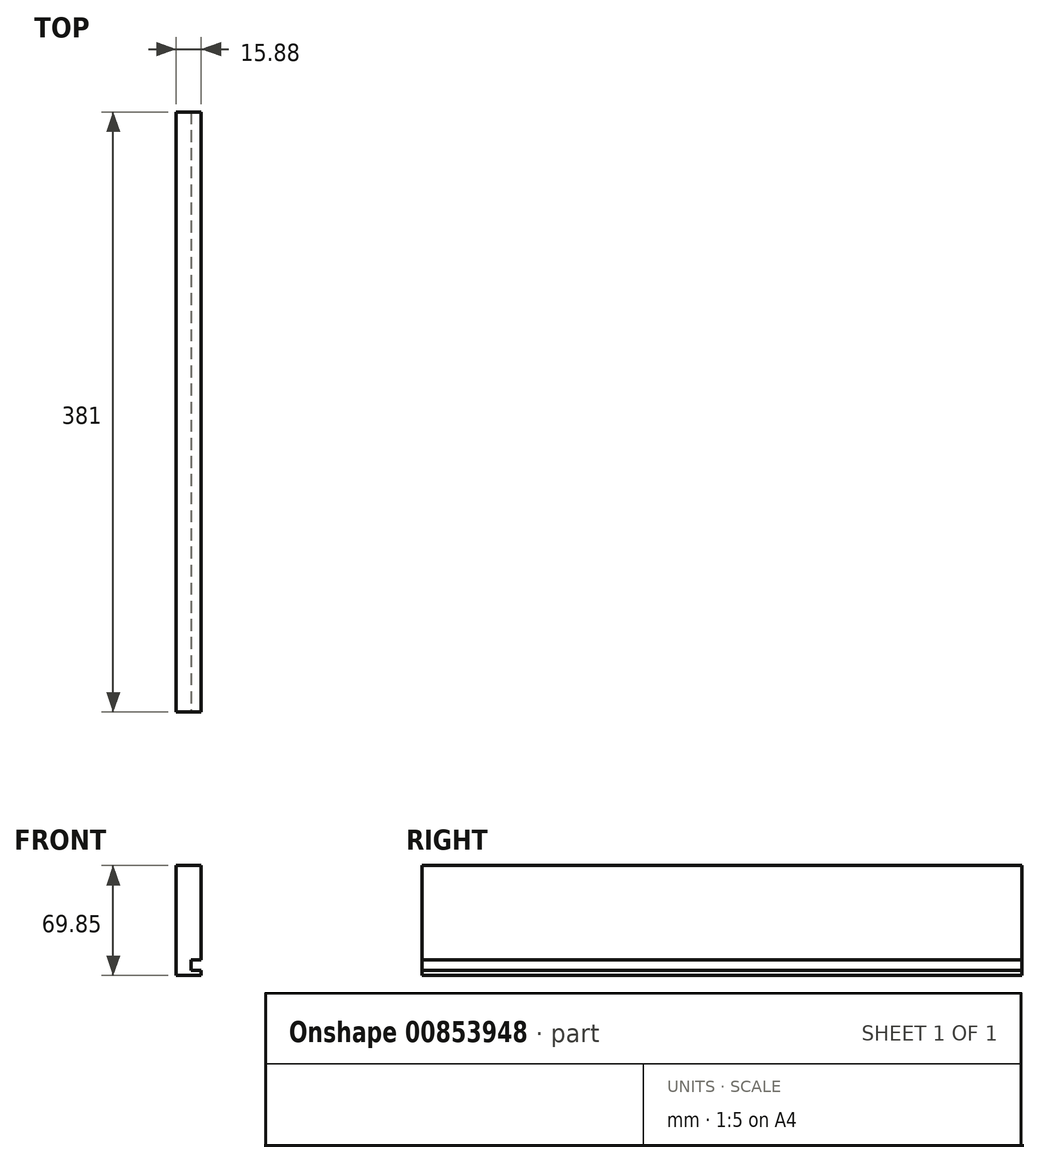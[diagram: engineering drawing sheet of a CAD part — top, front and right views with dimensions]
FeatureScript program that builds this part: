
annotation { "Feature Type Name" : "Feature", "Feature Type Description" : "" }
export const myFeature = defineFeature(function(context is Context, id is Id, definition is map)
    precondition{}
    {
        {
            var Q0;
            Q0=qCreatedBy(makeId("Right.planeOp"),FACE);
            var sketch = newSketch(context, id + "F0", { "sketchPlane" : qUnion([Q0])});
            skLineSegment(sketch, "E0.bottom", {"start": v(0, 69.85) * mm, "end": v(381, 69.85) * mm});
            skLineSegment(sketch, "E0.top", {"start": v(0, 0) * mm, "end": v(381, 0) * mm});
            skLineSegment(sketch, "E0.left", {"start": v(0, 69.85) * mm, "end": v(0, 0) * mm});
            skLineSegment(sketch, "E0.right", {"start": v(381, 69.85) * mm, "end": v(381, 0) * mm});
            skSolve(sketch);
        }
        {
            var Q0;
            Q0=makeQuery(id+"F0.imprint","IMPRINT",FACE,{"disambiguationData":[TD([[makeQuery(id+"F0.imprint","IMPRINT",EDGE,{"derivedFrom":sQuery(id+"F0.wireOp",EDGE,"E0.bottom")}),-1.0]])]});
            extrude(context, id + "F1", {"entities" : qUnion([Q0]), "depth" : 15.88 * mm, "offsetDistance" : 25.4 * mm});
        }
        {
            var Q0;
            Q0=makeQuery(id+"F1.opExtrude","SWEPT_FACE",FACE,{"disambiguationData":[OSD([sQuery(id+"F0.wireOp",EDGE,"E0.left")])]});
            var sketch = newSketch(context, id + "F2", { "sketchPlane" : qUnion([Q0])});
            skLineSegment(sketch, "E1.bottom", {"start": v(22.23, 9.78) * mm, "end": v(9.53, 9.78) * mm});
            skLineSegment(sketch, "E1.top", {"start": v(22.23, 3.18) * mm, "end": v(9.53, 3.17) * mm});
            skLineSegment(sketch, "E1.left", {"start": v(22.23, 9.78) * mm, "end": v(22.23, 3.18) * mm});
            skLineSegment(sketch, "E1.right", {"start": v(9.53, 9.78) * mm, "end": v(9.53, 3.17) * mm});
            skSolve(sketch);
        }
        {
            var Q0;
            {var subQ0=sQuery(id+"F2.wireOp",EDGE,"E1.right");Q0=makeQuery(id+"F2.imprint","IMPRINT",FACE,{"disambiguationData":[TD([[makeQuery(id+"F2.imprint","IMPRINT",EDGE,{"derivedFrom":subQ0}),1.0]])]});}
            extrude(context, id + "F3", {"entities" : qUnion([Q0]), "operationType" : NewBodyOperationType.REMOVE, "endBound" : BoundingType.UP_TO_NEXT, "oppositeDirection" : true, "depth" : 25.4 * mm, "offsetDistance" : 25.4 * mm});
        }
    });
